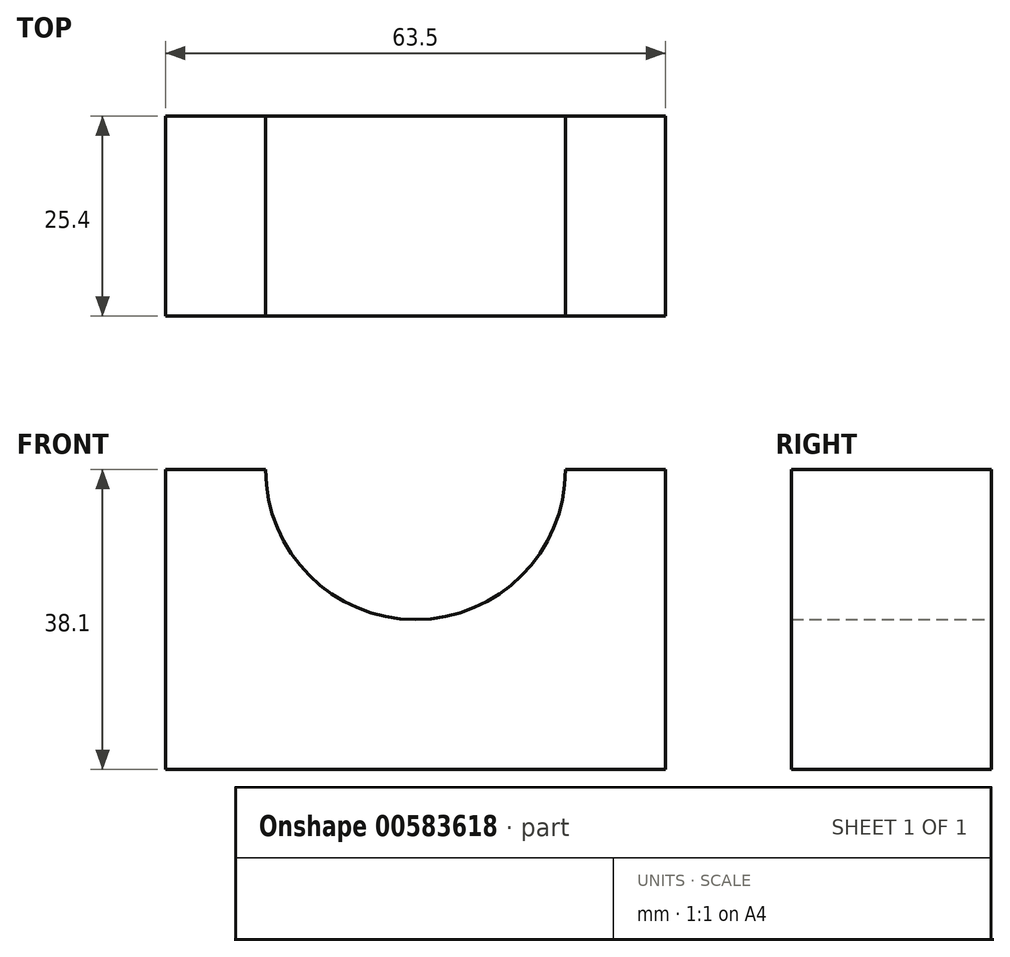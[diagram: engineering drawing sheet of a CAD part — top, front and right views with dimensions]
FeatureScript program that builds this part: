
annotation { "Feature Type Name" : "Feature", "Feature Type Description" : "" }
export const myFeature = defineFeature(function(context is Context, id is Id, definition is map)
    precondition{}
    {
        {
            var Q0;
            Q0=qCreatedBy(makeId("Front.planeOp"),FACE);
            var sketch = newSketch(context, id + "F0", { "sketchPlane" : qUnion([Q0])});
            skLineSegment(sketch, "E0", {"start": v(0, 0) * mm, "end": v(63.5, 0) * mm});
            skLineSegment(sketch, "E1", {"start": v(0, 0) * mm, "end": v(0, 38.1) * mm});
            skLineSegment(sketch, "E2", {"start": v(63.5, 0) * mm, "end": v(63.5, 38.1) * mm});
            skLineSegment(sketch, "E3", {"start": v(0, 38.1) * mm, "end": v(63.5, 38.1) * mm});
            skArc(sketch, "E4", {"start": v(12.7, 38.1) * mm, "mid": v(31.75, 19.05) * mm, "end": v(50.8, 38.1) * mm});
            skSolve(sketch);
        }
        {
            var Q0;
            Q0=makeQuery(id+"F0.imprint","IMPRINT",FACE,{"disambiguationData":[TD([[makeQuery(id+"F0.imprint","IMPRINT",EDGE,{"derivedFrom":sQuery(id+"F0.wireOp",EDGE,"E0")}),1.0]])]});
            extrude(context, id + "F1", {"entities" : qUnion([Q0]), "depth" : 25.4 * mm, "offsetDistance" : 25.4 * mm});
        }
    });
